# Revit family: LeL Oliver 3.0
name_source: partatom
category: Lighting Fixtures
units: mm (PartAtom-declared; Revit-internal decimal feet)

## family parameters
Always vertical = No
Cut with Voids When Loaded = No
Light Source = No
OmniClass Number = 23.80.70.00
OmniClass Title = Lighting
Part Type = Normal
Room Calculation Point = No
Round Connector Dimension = Use Diameter
Shared = No
Work Plane-Based = Yes

## types (7) — shared parameters
CCT = 3000 K
CRI = CRI80
Default Elevation = 1219 mm
Description = Outdoor Projectors
IK = IK09
IP = IP66
Lamp = LED
Manufacturer = L&L Luce&Light srl
Model = LV30
Rated Power supply = 230 V
URL = https://www.lucelight.it
Weight = 8.00 kg

## per-type parameters (varying)
| type | Apparent Load | Optic Group A | Optic Group B | Photometry | Wattage_2 |
| W 12°x49° 110W | 110 VA | Yes | No | LV30 Light source : W 12°x49° 110W | 110 W |
| V 5° 95W | 95 VA | No | Yes | LV30 Light source : V 5° 95W | 95 W |
| S 10° 110W | 110 VA | Yes | No | LV30 Light source : S 10° 110W | 110 W |
| M 19° 110W | 110 VA | Yes | No | LV30 Light source : M 19° 110W | 110 W |
| L 30° 110W | 110 VA | Yes | No | LV30 Light source : L 30° 110W | 110 W |
| K 54° 110W | 110 VA | Yes | No | LV30 Light source : K 54° 110W | 110 W |
| X 10°x65° 110W | 110 VA | Yes | No | LV30 Light source : X 10°x65° 110W | 110 W |

## geometry (parser evidence)
native form markers: Sweep x1
no freeform markers — native parametric forms only
